# Revit family: 12-51-005-DN050-300
name_source: partatom
category: Pipe Accessories
units: mm (PartAtom-declared; Revit-internal decimal feet)

## family parameters
Always vertical = No
Cut with Voids When Loaded = No
Part Type = Valve - Breaks Into
Round Connector Dimension = Use Diameter
Shared = No
Work Plane-Based = No

## types (12) — shared parameters
Body_Wallthickness = 15 mm  [stored 0.0492126 ft]
DN050_PN10/16 = 12-050-51-017
DN065_PN10/16 = 12-065-51-017
DN080_PN10/16 = 12-080-51-0146499
DN100_PN10/16 = 12-100-51-0146499
DN125_PN10/16 = 12-125-51-0146499
DN150_PN10/16 = 12-150-51-0146499
DN200_PN10 = 12-200-51-0046499
DN200_PN16 = 12-200-51-0146499
DN250_PN10 = 12-250-51-007
DN250_PN16 = 12-250-51-017
DN300_PN10 = 12-300-51-007
DN300_PN16 = 12-300-51-017
Description_ = AVK GATE VALVE, FLANGED/SPIGOT END
Ftc = 4 mm  [stored 0.0131234 ft]
Name_Height_reference = 10 mm  [stored 0.0328084 ft]
Rib_Thickness = 18 mm  [stored 0.0590551 ft]
Search_table = 12-51-005-DN050-300
URL product pages = https://www.avkvalves.com
zero-valued in all types: Bottom_Reference

## per-type parameters (varying)
- DN050_PN10/16: At=45 mm  [stored 0.147638 ft]; Body_Height=101 mm; Body_depth=90 mm; Body_width=60 mm; Body_width_ref=120 mm; Bonnet_Flange_Depth=118 mm; Bonnet_Flange_Width=82 mm; Bonnet_Flange_cut=8 mm  [stored 0.0262467 ft]; Bonnet_Flange_thickness=15 mm  [stored 0.0492126 ft]; Bonnet_Height=41 mm  [stored 0.134514 ft]; Bonnet_Reference_height=91 mm; Bonnet_Thickness=61 mm; Bt=61 mm; Bt_2=54 mm  [stored 0.177165 ft]; CL _Thickness=19 mm  [stored 0.062336 ft]; CL_Height=50 mm  [stored 0.164042 ft]; Cut_Reference=488 mm; D=33 mm  [stored 0.108268 ft]; D1=10 mm  [stored 0.0328084 ft]; D2=29 mm  [stored 0.0951444 ft]; D_ref=66 mm; E=11 mm  [stored 0.0360892 ft]; F=7 mm  [stored 0.0229659 ft]; F1=17 mm  [stored 0.0557743 ft]; Fillet_Thickness=6 mm  [stored 0.019685 ft]; Flange_OR=83 mm; Flange_Thickness=19 mm  [stored 0.062336 ft]; Flange_Thickness_cut=29 mm  [stored 0.0951444 ft]; Ftc_reference_height=83 mm; H=241 mm; H1=212 mm; H3=324 mm; Horizontal_Flange_width=166 mm; ID (Radius)=25 mm  [stored 0.082021 ft]; L=244 mm; L1=121 mm; L_Dia=50 mm  [stored 0.164042 ft]; Name_Reference=71 mm; Name_Width=30 mm  [stored 0.0984252 ft]; Neck_H=62 mm; Neck_T=17 mm  [stored 0.0557743 ft]; Neck_T2=15 mm  [stored 0.0492126 ft]; Nominal Diameter (DN)=50 mm  [stored 0.164042 ft]; R1tv=825 mm; R2f=15 mm  [stored 0.0492126 ft]; RF_Dia=50 mm  [stored 0.164042 ft]; Rf=277 mm; Rib_Height_Reference_1=120 mm; Rib_Height_Reference_2=110 mm; Rib_Height_Reference_3=100 mm; Rib_Height_Reference_4=60 mm; Rib_Width_1=30 mm  [stored 0.0984252 ft]; Rib_Width_2=30 mm  [stored 0.0984252 ft]; Rib_Width_3=30 mm  [stored 0.0984252 ft]; Rib_depth_1=30 mm  [stored 0.0984252 ft]; Rib_depth_2=30 mm  [stored 0.0984252 ft]; Rib_depth_3=30 mm  [stored 0.0984252 ft]; Rt=275 mm
- DN065_PN10/16: At=54 mm  [stored 0.177165 ft]; Body_Height=115 mm; Body_depth=107 mm; Body_width=55 mm; Body_width_ref=110 mm; Bonnet_Flange_Depth=135 mm; Bonnet_Flange_Width=65 mm; Bonnet_Flange_cut=8 mm  [stored 0.0262467 ft]; Bonnet_Flange_thickness=15 mm  [stored 0.0492126 ft]; Bonnet_Height=47 mm  [stored 0.154199 ft]; Bonnet_Reference_height=105 mm; Bonnet_Thickness=56 mm; Bt=56 mm; Bt_2=49 mm  [stored 0.160761 ft]; CL _Thickness=17 mm  [stored 0.0557743 ft]; CL_Height=59 mm; Cut_Reference=528 mm; D=41 mm  [stored 0.134514 ft]; D1=10 mm  [stored 0.0328084 ft]; D2=34 mm  [stored 0.111549 ft]; D_ref=82 mm; E=11 mm  [stored 0.0360892 ft]; F=9 mm; F1=20 mm  [stored 0.0656168 ft]; Fillet_Thickness=6 mm  [stored 0.019685 ft]; Flange_OR=93 mm; Flange_Thickness=19 mm  [stored 0.062336 ft]; Flange_Thickness_cut=30 mm  [stored 0.0984252 ft]; Ftc_reference_height=93 mm; H=271 mm; H1=237 mm; H3=364 mm; Horizontal_Flange_width=186 mm; ID (Radius)=33 mm  [stored 0.108268 ft]; L=264 mm; L1=130 mm; L_Dia=65 mm; Name_Reference=96 mm; Name_Width=28 mm  [stored 0.0918635 ft]; Neck_H=64 mm; Neck_T=15 mm  [stored 0.0492126 ft]; Neck_T2=13 mm; Nominal Diameter (DN)=65 mm; R1tv=930 mm; R2f=15 mm  [stored 0.0492126 ft]; RF_Dia=59 mm; Rf=310 mm; Rib_Height_Reference_1=120 mm; Rib_Height_Reference_2=110 mm; Rib_Height_Reference_3=100 mm; Rib_Height_Reference_4=75 mm; Rib_Width_1=28 mm  [stored 0.0918635 ft]; Rib_Width_2=28 mm  [stored 0.0918635 ft]; Rib_Width_3=28 mm  [stored 0.0918635 ft]; Rib_depth_1=28 mm  [stored 0.0918635 ft]; Rib_depth_2=28 mm  [stored 0.0918635 ft]; Rib_depth_3=28 mm  [stored 0.0918635 ft]; Rt=310 mm
- DN080_PN10/16: At=70 mm; Body_Height=108 mm; Body_depth=140 mm; Body_width=60 mm; Body_width_ref=120 mm; Bonnet_Flange_Depth=171 mm; Bonnet_Flange_Width=76 mm; Bonnet_Flange_cut=8 mm  [stored 0.0262467 ft]; Bonnet_Flange_thickness=15 mm  [stored 0.0492126 ft]; Bonnet_Height=50 mm  [stored 0.164042 ft]; Bonnet_Reference_height=98 mm; Bonnet_Thickness=61 mm; Bt=61 mm; Bt_2=54 mm  [stored 0.177165 ft]; CL _Thickness=19 mm  [stored 0.062336 ft]; CL_Height=75 mm; Cut_Reference=548 mm; D=49 mm  [stored 0.160761 ft]; D1=10 mm  [stored 0.0328084 ft]; D2=34 mm  [stored 0.111549 ft]; D_ref=98 mm; E=15 mm  [stored 0.0492126 ft]; F=9 mm; F1=20 mm  [stored 0.0656168 ft]; Fillet_Thickness=6 mm  [stored 0.019685 ft]; Flange_OR=100 mm; Flange_Thickness=19 mm  [stored 0.062336 ft]; Flange_Thickness_cut=30 mm  [stored 0.0984252 ft]; Ftc_reference_height=100 mm; H=297 mm; H1=263 mm; H3=397 mm; Horizontal_Flange_width=200 mm; ID (Radius)=40 mm  [stored 0.131234 ft]; L=274 mm; L1=127 mm; L_Dia=80 mm; Name_Reference=90 mm; Name_Width=30 mm  [stored 0.0984252 ft]; Neck_H=80 mm; Neck_T=17 mm  [stored 0.0557743 ft]; Neck_T2=15 mm  [stored 0.0492126 ft]; Nominal Diameter (DN)=80 mm; R1tv=1000 mm; R2f=15 mm  [stored 0.0492126 ft]; RF_Dia=66 mm; Rf=333 mm; Rib_Height_Reference_1=120 mm; Rib_Height_Reference_2=110 mm; Rib_Height_Reference_3=100 mm; Rib_Height_Reference_4=85 mm; Rib_Width_1=30 mm  [stored 0.0984252 ft]; Rib_Width_2=30 mm  [stored 0.0984252 ft]; Rib_Width_3=30 mm  [stored 0.0984252 ft]; Rib_depth_1=30 mm  [stored 0.0984252 ft]; Rib_depth_2=30 mm  [stored 0.0984252 ft]; Rib_depth_3=30 mm  [stored 0.0984252 ft]; Rt=333 mm
- DN100_PN10/16: At=83 mm; Body_Height=122 mm; Body_depth=166 mm; Body_width=60 mm; Body_width_ref=120 mm; Bonnet_Flange_Depth=192 mm; Bonnet_Flange_Width=81 mm; Bonnet_Flange_cut=8 mm  [stored 0.0262467 ft]; Bonnet_Flange_thickness=15 mm  [stored 0.0492126 ft]; Bonnet_Height=55 mm; Bonnet_Reference_height=112 mm; Bonnet_Thickness=61 mm; Bt=61 mm; Bt_2=54 mm  [stored 0.177165 ft]; CL _Thickness=19 mm  [stored 0.062336 ft]; CL_Height=88 mm; Cut_Reference=588 mm; D=59 mm; D1=10 mm  [stored 0.0328084 ft]; D2=38 mm  [stored 0.124672 ft]; D_ref=118 mm; E=15 mm  [stored 0.0492126 ft]; F=10 mm  [stored 0.0328084 ft]; F1=22 mm  [stored 0.0721785 ft]; Fillet_Thickness=6 mm  [stored 0.019685 ft]; Flange_OR=110 mm; Flange_Thickness=19 mm  [stored 0.062336 ft]; Flange_Thickness_cut=30 mm  [stored 0.0984252 ft]; Ftc_reference_height=110 mm; H=334 mm; H1=296 mm; H3=444 mm; Horizontal_Flange_width=220 mm; ID (Radius)=50 mm  [stored 0.164042 ft]; L=294 mm; L1=133 mm; L_Dia=100 mm; Name_Reference=101 mm; Name_Width=30 mm  [stored 0.0984252 ft]; Neck_H=86 mm; Neck_T=17 mm  [stored 0.0557743 ft]; Neck_T2=15 mm  [stored 0.0492126 ft]; Nominal Diameter (DN)=100 mm; R1tv=1100 mm; R2f=15 mm  [stored 0.0492126 ft]; RF_Dia=78 mm; Rf=367 mm; Rib_Height_Reference_1=120 mm; Rib_Height_Reference_2=110 mm; Rib_Height_Reference_3=100 mm; Rib_Height_Reference_4=90 mm; Rib_Width_1=30 mm  [stored 0.0984252 ft]; Rib_Width_2=30 mm  [stored 0.0984252 ft]; Rib_Width_3=30 mm  [stored 0.0984252 ft]; Rib_depth_1=30 mm  [stored 0.0984252 ft]; Rib_depth_2=30 mm  [stored 0.0984252 ft]; Rib_depth_3=30 mm  [stored 0.0984252 ft]; Rt=367 mm
- DN125_PN10/16: At=97 mm; Body_Height=137 mm; Body_depth=194 mm; Body_width=65 mm; Body_width_ref=130 mm; Bonnet_Flange_Depth=220 mm; Bonnet_Flange_Width=83 mm; Bonnet_Flange_cut=8 mm  [stored 0.0262467 ft]; Bonnet_Flange_thickness=15 mm  [stored 0.0492126 ft]; Bonnet_Height=63 mm; Bonnet_Reference_height=127 mm; Bonnet_Thickness=66 mm; Bt=66 mm; Bt_2=59 mm; CL _Thickness=22 mm  [stored 0.0721785 ft]; CL_Height=102 mm; Cut_Reference=638 mm; D=72 mm; D1=10 mm  [stored 0.0328084 ft]; D2=38 mm  [stored 0.124672 ft]; D_ref=144 mm; E=15 mm  [stored 0.0492126 ft]; F=10 mm  [stored 0.0328084 ft]; F1=22 mm  [stored 0.0721785 ft]; Fillet_Thickness=6 mm  [stored 0.019685 ft]; Flange_OR=125 mm; Flange_Thickness=19 mm  [stored 0.062336 ft]; Flange_Thickness_cut=31 mm  [stored 0.101706 ft]; Ftc_reference_height=125 mm; H=376 mm; H1=338 mm; H3=501 mm; Horizontal_Flange_width=250 mm; ID (Radius)=63 mm; L=319 mm; L1=149 mm; L_Dia=125 mm; Name_Reference=114 mm; Name_Width=33 mm  [stored 0.108268 ft]; Neck_H=99 mm; Neck_T=20 mm  [stored 0.0656168 ft]; Neck_T2=18 mm  [stored 0.0590551 ft]; Nominal Diameter (DN)=125 mm; R1tv=1250 mm; R2f=15 mm  [stored 0.0492126 ft]; RF_Dia=92 mm; Rf=417 mm; Rib_Height_Reference_1=120 mm; Rib_Height_Reference_2=110 mm; Rib_Height_Reference_3=100 mm; Rib_Height_Reference_4=120 mm; Rib_Width_1=33 mm  [stored 0.108268 ft]; Rib_Width_2=33 mm  [stored 0.108268 ft]; Rib_Width_3=33 mm  [stored 0.108268 ft]; Rib_depth_1=33 mm  [stored 0.108268 ft]; Rib_depth_2=33 mm  [stored 0.108268 ft]; Rib_depth_3=33 mm  [stored 0.108268 ft]; Rt=417 mm
- DN150_PN10/16: At=121 mm; Body_Height=172 mm; Body_depth=242 mm; Body_width=95 mm; Body_width_ref=190 mm; Bonnet_Flange_Depth=272 mm; Bonnet_Flange_Width=116 mm; Bonnet_Flange_cut=8 mm  [stored 0.0262467 ft]; Bonnet_Flange_thickness=15 mm  [stored 0.0492126 ft]; Bonnet_Height=71 mm; Bonnet_Reference_height=162 mm; Bonnet_Thickness=97 mm; Bt=97 mm; Bt_2=89 mm; CL _Thickness=34 mm  [stored 0.111549 ft]; CL_Height=126 mm; Cut_Reference=688 mm; D=85 mm; D1=10 mm  [stored 0.0328084 ft]; D2=38 mm  [stored 0.124672 ft]; D_ref=170 mm; E=15 mm  [stored 0.0492126 ft]; F=10 mm  [stored 0.0328084 ft]; F1=22 mm  [stored 0.0721785 ft]; Fillet_Thickness=12 mm  [stored 0.0393701 ft]; Flange_OR=142 mm; Flange_Thickness=19 mm  [stored 0.062336 ft]; Flange_Thickness_cut=34 mm  [stored 0.111549 ft]; Ftc_reference_height=142 mm; H=448 mm; H1=410 mm; H3=591 mm; Horizontal_Flange_width=286 mm; ID (Radius)=75 mm; L=344 mm; L1=160 mm; L_Dia=150 mm; Name_Reference=143 mm; Name_Width=48 mm  [stored 0.15748 ft]; Neck_H=112 mm; Neck_T=32 mm  [stored 0.104987 ft]; Neck_T2=30 mm  [stored 0.0984252 ft]; Nominal Diameter (DN)=150 mm; R1tv=1420 mm; R2f=30 mm  [stored 0.0984252 ft]; RF_Dia=106 mm; Rf=477 mm; Rib_Height_Reference_1=120 mm; Rib_Height_Reference_2=110 mm; Rib_Height_Reference_3=100 mm; Rib_Height_Reference_4=150 mm; Rib_Width_1=48 mm  [stored 0.15748 ft]; Rib_Width_2=48 mm  [stored 0.15748 ft]; Rib_Width_3=48 mm  [stored 0.15748 ft]; Rib_depth_1=48 mm  [stored 0.15748 ft]; Rib_depth_2=48 mm  [stored 0.15748 ft]; Rib_depth_3=48 mm  [stored 0.15748 ft]; Rt=473 mm
- DN200_PN10: At=147 mm; Body_Height=250 mm; Body_depth=294 mm; Body_width=108 mm; Body_width_ref=216 mm; Bonnet_Flange_Depth=332 mm; Bonnet_Flange_Width=132 mm; Bonnet_Flange_cut=13 mm; Bonnet_Flange_thickness=25 mm  [stored 0.082021 ft]; Bonnet_Height=85 mm; Bonnet_Reference_height=240 mm; Bonnet_Thickness=110 mm; Bt=110 mm; Bt_2=102 mm; CL _Thickness=34 mm  [stored 0.111549 ft]; CL_Height=152 mm; Cut_Reference=788 mm; D=111 mm; D1=10 mm  [stored 0.0328084 ft]; D2=42 mm  [stored 0.137795 ft]; D_ref=222 mm; E=15 mm  [stored 0.0492126 ft]; F=12 mm  [stored 0.0393701 ft]; F1=28 mm  [stored 0.0918635 ft]; Fillet_Thickness=24 mm  [stored 0.0787402 ft]; Flange_OR=170 mm; Flange_Thickness=20 mm  [stored 0.0656168 ft]; Flange_Thickness_cut=35 mm  [stored 0.114829 ft]; Ftc_reference_height=170 mm; H=562 mm; H1=520 mm; H3=732 mm; Horizontal_Flange_width=340 mm; ID (Radius)=100 mm; L=394 mm; L1=187 mm; L_Dia=200 mm; Name_Reference=183 mm; Name_Width=54 mm  [stored 0.177165 ft]; Neck_H=118 mm; Neck_T=32 mm  [stored 0.104987 ft]; Neck_T2=30 mm  [stored 0.0984252 ft]; Nominal Diameter (DN)=200 mm; R1tv=1700 mm; R2f=60 mm; RF_Dia=133 mm; Rf=567 mm; Rib_Height_Reference_1=120 mm; Rib_Height_Reference_2=110 mm; Rib_Height_Reference_3=100 mm; Rib_Height_Reference_4=180 mm; Rib_Width_1=54 mm  [stored 0.177165 ft]; Rib_Width_2=54 mm  [stored 0.177165 ft]; Rib_Width_3=54 mm  [stored 0.177165 ft]; Rib_depth_1=54 mm  [stored 0.177165 ft]; Rib_depth_2=54 mm  [stored 0.177165 ft]; Rib_depth_3=54 mm  [stored 0.177165 ft]; Rt=567 mm
- DN200_PN16: At=147 mm; Body_Height=250 mm; Body_depth=294 mm; Body_width=108 mm; Body_width_ref=216 mm; Bonnet_Flange_Depth=332 mm; Bonnet_Flange_Width=132 mm; Bonnet_Flange_cut=13 mm; Bonnet_Flange_thickness=25 mm  [stored 0.082021 ft]; Bonnet_Height=85 mm; Bonnet_Reference_height=240 mm; Bonnet_Thickness=110 mm; Bt=110 mm; Bt_2=102 mm; CL _Thickness=34 mm  [stored 0.111549 ft]; CL_Height=152 mm; Cut_Reference=788 mm; D=111 mm; D1=10 mm  [stored 0.0328084 ft]; D2=42 mm  [stored 0.137795 ft]; D_ref=222 mm; E=15 mm  [stored 0.0492126 ft]; F=12 mm  [stored 0.0393701 ft]; F1=28 mm  [stored 0.0918635 ft]; Fillet_Thickness=24 mm  [stored 0.0787402 ft]; Flange_OR=170 mm; Flange_Thickness=20 mm  [stored 0.0656168 ft]; Flange_Thickness_cut=35 mm  [stored 0.114829 ft]; Ftc_reference_height=170 mm; H=562 mm; H1=520 mm; H3=732 mm; Horizontal_Flange_width=340 mm; ID (Radius)=100 mm; L=394 mm; L1=187 mm; L_Dia=200 mm; Name_Reference=183 mm; Name_Width=54 mm  [stored 0.177165 ft]; Neck_H=118 mm; Neck_T=32 mm  [stored 0.104987 ft]; Neck_T2=30 mm  [stored 0.0984252 ft]; Nominal Diameter (DN)=200 mm; R1tv=1700 mm; R2f=60 mm; RF_Dia=133 mm; Rf=567 mm; Rib_Height_Reference_1=120 mm; Rib_Height_Reference_2=110 mm; Rib_Height_Reference_3=100 mm; Rib_Height_Reference_4=180 mm; Rib_Width_1=54 mm  [stored 0.177165 ft]; Rib_Width_2=54 mm  [stored 0.177165 ft]; Rib_Width_3=54 mm  [stored 0.177165 ft]; Rib_depth_1=54 mm  [stored 0.177165 ft]; Rib_depth_2=54 mm  [stored 0.177165 ft]; Rib_depth_3=54 mm  [stored 0.177165 ft]; Rt=567 mm
- DN250_PN10: At=171 mm; Body_Height=305 mm; Body_depth=342 mm; Body_width=124 mm; Body_width_ref=248 mm; Bonnet_Flange_Depth=372 mm; Bonnet_Flange_Width=158 mm; Bonnet_Flange_cut=13 mm; Bonnet_Flange_thickness=25 mm  [stored 0.082021 ft]; Bonnet_Height=100 mm; Bonnet_Reference_height=295 mm; Bonnet_Thickness=126 mm; Bt=126 mm; Bt_2=118 mm; CL _Thickness=42 mm  [stored 0.137795 ft]; CL_Height=176 mm; Cut_Reference=888 mm; D=137 mm; D1=15 mm  [stored 0.0492126 ft]; D2=47 mm  [stored 0.154199 ft]; D_ref=274 mm; E=13 mm; F=14 mm  [stored 0.0459318 ft]; F1=31 mm  [stored 0.101706 ft]; Fillet_Thickness=24 mm  [stored 0.0787402 ft]; Flange_OR=200 mm; Flange_Thickness=22 mm  [stored 0.0721785 ft]; Flange_Thickness_cut=38 mm  [stored 0.124672 ft]; Ftc_reference_height=200 mm; H=664 mm; H1=617 mm; H3=864 mm; Horizontal_Flange_width=400 mm; ID (Radius)=125 mm; L=444 mm; L1=179 mm; L_Dia=250 mm; Name_Reference=270 mm; Name_Width=62 mm; Neck_H=136 mm; Neck_T=40 mm  [stored 0.131234 ft]; Neck_T2=38 mm  [stored 0.124672 ft]; Nominal Diameter (DN)=250 mm; R1tv=2000 mm; R2f=60 mm; RF_Dia=160 mm; Rf=667 mm; Rib_Height_Reference_1=90 mm; Rib_Height_Reference_2=110 mm; Rib_Height_Reference_3=100 mm; Rib_Height_Reference_4=200 mm; Rib_Width_1=140 mm; Rib_Width_2=140 mm; Rib_Width_3=62 mm; Rib_depth_1=372 mm; Rib_depth_2=62 mm; Rib_depth_3=62 mm; Rt=667 mm
- DN250_PN16: At=171 mm; Body_Height=305 mm; Body_depth=342 mm; Body_width=124 mm; Body_width_ref=248 mm; Bonnet_Flange_Depth=372 mm; Bonnet_Flange_Width=158 mm; Bonnet_Flange_cut=13 mm; Bonnet_Flange_thickness=25 mm  [stored 0.082021 ft]; Bonnet_Height=100 mm; Bonnet_Reference_height=295 mm; Bonnet_Thickness=126 mm; Bt=126 mm; Bt_2=118 mm; CL _Thickness=42 mm  [stored 0.137795 ft]; CL_Height=176 mm; Cut_Reference=888 mm; D=137 mm; D1=15 mm  [stored 0.0492126 ft]; D2=47 mm  [stored 0.154199 ft]; D_ref=274 mm; E=13 mm; F=14 mm  [stored 0.0459318 ft]; F1=31 mm  [stored 0.101706 ft]; Fillet_Thickness=24 mm  [stored 0.0787402 ft]; Flange_OR=200 mm; Flange_Thickness=22 mm  [stored 0.0721785 ft]; Flange_Thickness_cut=37 mm; Ftc_reference_height=200 mm; H=664 mm; H1=617 mm; H3=864 mm; Horizontal_Flange_width=400 mm; ID (Radius)=125 mm; L=444 mm; L1=179 mm; L_Dia=250 mm; Name_Reference=270 mm; Name_Width=62 mm; Neck_H=136 mm; Neck_T=40 mm  [stored 0.131234 ft]; Neck_T2=38 mm  [stored 0.124672 ft]; Nominal Diameter (DN)=250 mm; R1tv=2000 mm; R2f=60 mm; RF_Dia=160 mm; Rf=667 mm; Rib_Height_Reference_1=90 mm; Rib_Height_Reference_2=110 mm; Rib_Height_Reference_3=100 mm; Rib_Height_Reference_4=200 mm; Rib_Width_1=140 mm; Rib_Width_2=140 mm; Rib_Width_3=62 mm; Rib_depth_1=372 mm; Rib_depth_2=62 mm; Rib_depth_3=62 mm; Rt=667 mm
- DN300_PN10: At=209 mm; Body_Height=370 mm; Body_depth=418 mm; Body_width=140 mm; Body_width_ref=280 mm; Bonnet_Flange_Depth=432 mm; Bonnet_Flange_Width=206 mm; Bonnet_Flange_cut=18 mm  [stored 0.0590551 ft]; Bonnet_Flange_thickness=35 mm  [stored 0.114829 ft]; Bonnet_Height=114 mm; Bonnet_Reference_height=360 mm; Bonnet_Thickness=143 mm; Bt=143 mm; Bt_2=134 mm; CL _Thickness=50 mm  [stored 0.164042 ft]; CL_Height=214 mm; Cut_Reference=988 mm; D=163 mm; D1=15 mm  [stored 0.0492126 ft]; D2=47 mm  [stored 0.154199 ft]; D_ref=326 mm; E=13 mm; F=14 mm  [stored 0.0459318 ft]; F1=31 mm  [stored 0.101706 ft]; Fillet_Thickness=24 mm  [stored 0.0787402 ft]; Flange_OR=228 mm; Flange_Thickness=25 mm  [stored 0.082021 ft]; Flange_Thickness_cut=39 mm  [stored 0.127953 ft]; Ftc_reference_height=228 mm; H=740 mm; H1=693 mm; H3=968 mm; Horizontal_Flange_width=456 mm; ID (Radius)=150 mm; L=494 mm; L1=204 mm; L_Dia=300 mm; Name_Reference=250 mm; Name_Width=70 mm; Neck_H=109 mm; Neck_T=48 mm  [stored 0.15748 ft]; Neck_T2=46 mm  [stored 0.150919 ft]; Nominal Diameter (DN)=300 mm; R1tv=2280 mm; R2f=60 mm; RF_Dia=185 mm; Rf=760 mm; Rib_Height_Reference_1=178 mm; Rib_Height_Reference_2=285 mm; Rib_Height_Reference_3=150 mm; Rib_Height_Reference_4=300 mm; Rib_Width_1=168 mm; Rib_Width_2=168 mm; Rib_Width_3=70 mm; Rib_depth_1=432 mm; Rib_depth_2=432 mm; Rib_depth_3=70 mm; Rt=760 mm
- DN300_PN16: At=209 mm; Body_Height=370 mm; Body_depth=418 mm; Body_width=140 mm; Body_width_ref=280 mm; Bonnet_Flange_Depth=432 mm; Bonnet_Flange_Width=206 mm; Bonnet_Flange_cut=18 mm  [stored 0.0590551 ft]; Bonnet_Flange_thickness=35 mm  [stored 0.114829 ft]; Bonnet_Height=114 mm; Bonnet_Reference_height=360 mm; Bonnet_Thickness=143 mm; Bt=143 mm; Bt_2=134 mm; CL _Thickness=50 mm  [stored 0.164042 ft]; CL_Height=214 mm; Cut_Reference=988 mm; D=163 mm; D1=15 mm  [stored 0.0492126 ft]; D2=47 mm  [stored 0.154199 ft]; D_ref=326 mm; E=13 mm; F=14 mm  [stored 0.0459318 ft]; F1=31 mm  [stored 0.101706 ft]; Fillet_Thickness=24 mm  [stored 0.0787402 ft]; Flange_OR=228 mm; Flange_Thickness=25 mm  [stored 0.082021 ft]; Flange_Thickness_cut=39 mm  [stored 0.127953 ft]; Ftc_reference_height=228 mm; H=740 mm; H1=693 mm; H3=968 mm; Horizontal_Flange_width=456 mm; ID (Radius)=150 mm; L=494 mm; L1=204 mm; L_Dia=300 mm; Name_Reference=250 mm; Name_Width=70 mm; Neck_H=109 mm; Neck_T=48 mm  [stored 0.15748 ft]; Neck_T2=46 mm  [stored 0.150919 ft]; Nominal Diameter (DN)=300 mm; R1tv=2280 mm; R2f=60 mm; RF_Dia=185 mm; Rf=760 mm; Rib_Height_Reference_1=178 mm; Rib_Height_Reference_2=285 mm; Rib_Height_Reference_3=150 mm; Rib_Height_Reference_4=300 mm; Rib_Width_1=168 mm; Rib_Width_2=168 mm; Rib_Width_3=70 mm; Rib_depth_1=432 mm; Rib_depth_2=432 mm; Rib_depth_3=70 mm; Rt=760 mm

note: [stored X ft] marks values corroborated as IEEE doubles in the binary element streams (Revit-internal decimal feet)

## geometry (parser evidence)
native form markers: Sweep x3
no freeform markers — native parametric forms only
